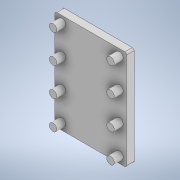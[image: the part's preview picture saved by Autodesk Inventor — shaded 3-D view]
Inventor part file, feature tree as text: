
AUTODESK INVENTOR PART (.ipt)
format: ipt  version: 2022 (Build 260153000, 153)  size: 161,280 bytes
history: native  units: in
note: dims shown in document units (in); Inventor stores cm internally (conversion verified against a paired STEP export)
features: sketch x3, extrude x2
ambient origin geometry x8: Origin, YZ Plane, XZ Plane, XY Plane, X Axis, Y Axis, Z Axis, Center Point
bodies: Solid1 (feature_tree)
feature tree (5):
  extrude  "Extrusion1"  Depth=1.0in
  extrude  "Extrusion2"  Depth=0.52in
  sketch  "Sketch3"  dims[d7=1.0in d8=1.0in d9=1.0in d10=0.52in d11=0.52in d12=1.0in d13=1.0in d14=0.52in d15=0.125in d16=0.125in d17=0.125in d18=0.52in d19=0.0in d20=1.145in d21=0.0in]
  sketch  "Sketch1"  dims[d3=1.0in d4=1.0in]
  sketch  "Sketch2"  dims[d5=0.52in d6=1.0in]
